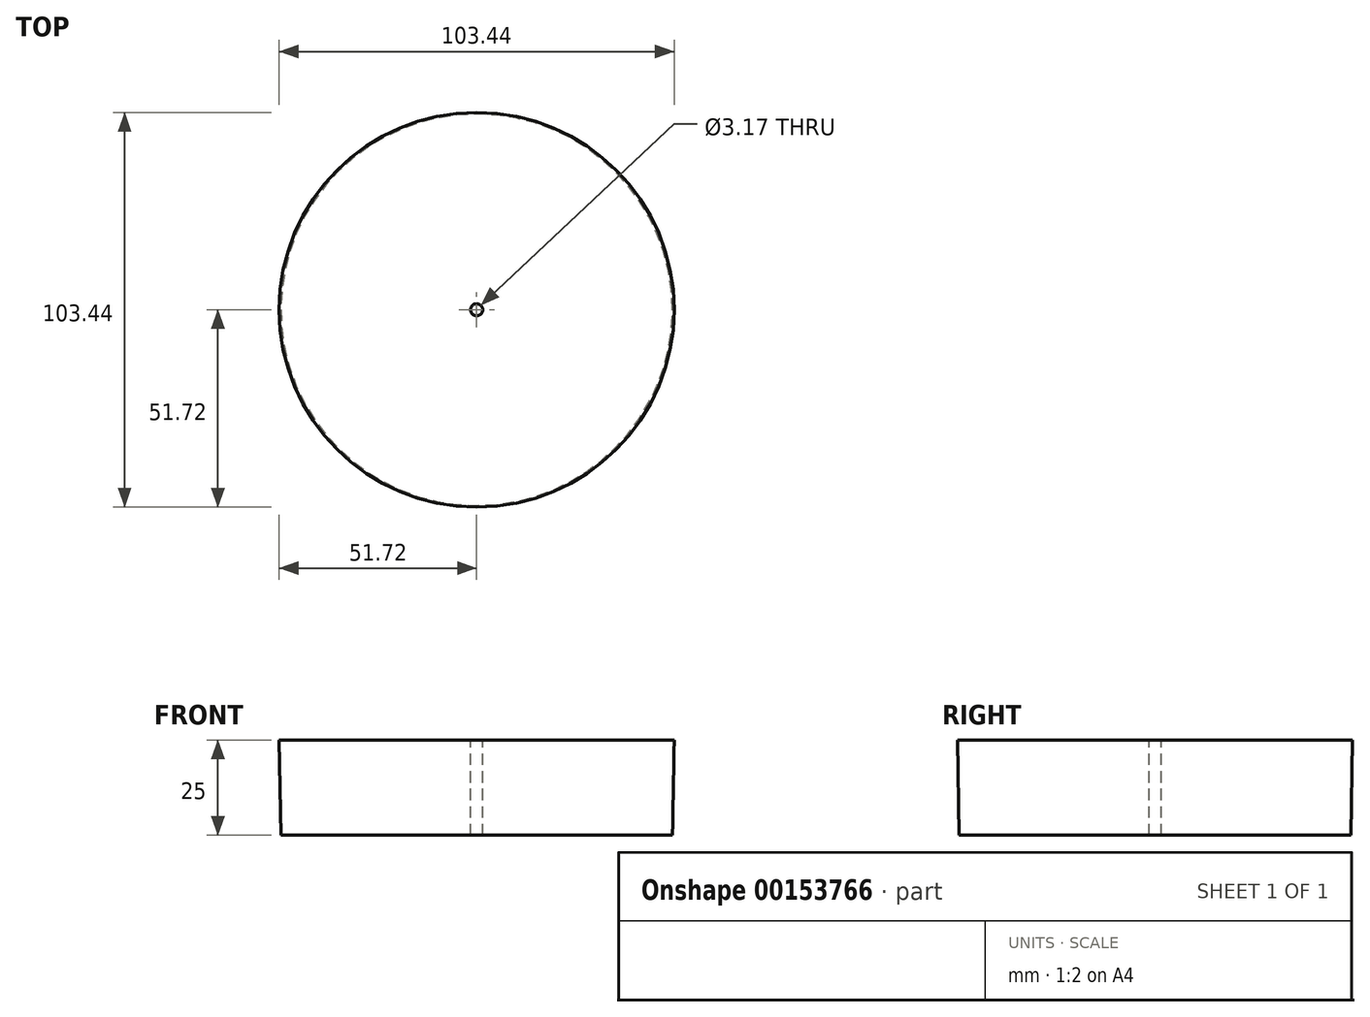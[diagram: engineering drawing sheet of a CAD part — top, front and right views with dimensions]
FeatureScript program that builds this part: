
annotation { "Feature Type Name" : "Feature", "Feature Type Description" : "" }
export const myFeature = defineFeature(function(context is Context, id is Id, definition is map)
    precondition{}
    {
        {
            var Q0;
            Q0=qCreatedBy(makeId("Top.planeOp"),FACE);
            var sketch = newSketch(context, id + "F0", { "sketchPlane" : qUnion([Q0])});
            skCircle(sketch, "E0", {"center": v(0, 0) * mm, "radius": 51.28 * mm});
            skSolve(sketch);
        }
        {
            var Q0;
            Q0 = qSketchRegion(id + "F0", true);
            extrude(context, id + "F1", {"entities" : qUnion([Q0]), "depth" : 25 * mm, "hasDraft" : true, "draftAngle" : 1 * degree});
        }
        {
            var Q0;
            Q0=makeQuery(id+"F1.opExtrude","CAP_FACE",FACE,{"disambiguationData":[OSD([sQuery(id+"F0.wireOp",EDGE,"E0")])],"isStart":false});
            var sketch = newSketch(context, id + "F2", { "sketchPlane" : qUnion([Q0])});
            skCircle(sketch, "E1", {"center": v(0, 0) * mm, "radius": 1.59 * mm});
            skSolve(sketch);
        }
        {
            var Q0;
            Q0 = qSketchRegion(id + "F2", true);
            extrude(context, id + "F3", {"entities" : qUnion([Q0]), "operationType" : NewBodyOperationType.REMOVE, "oppositeDirection" : true, "depth" : 25 * mm});
        }
    });
